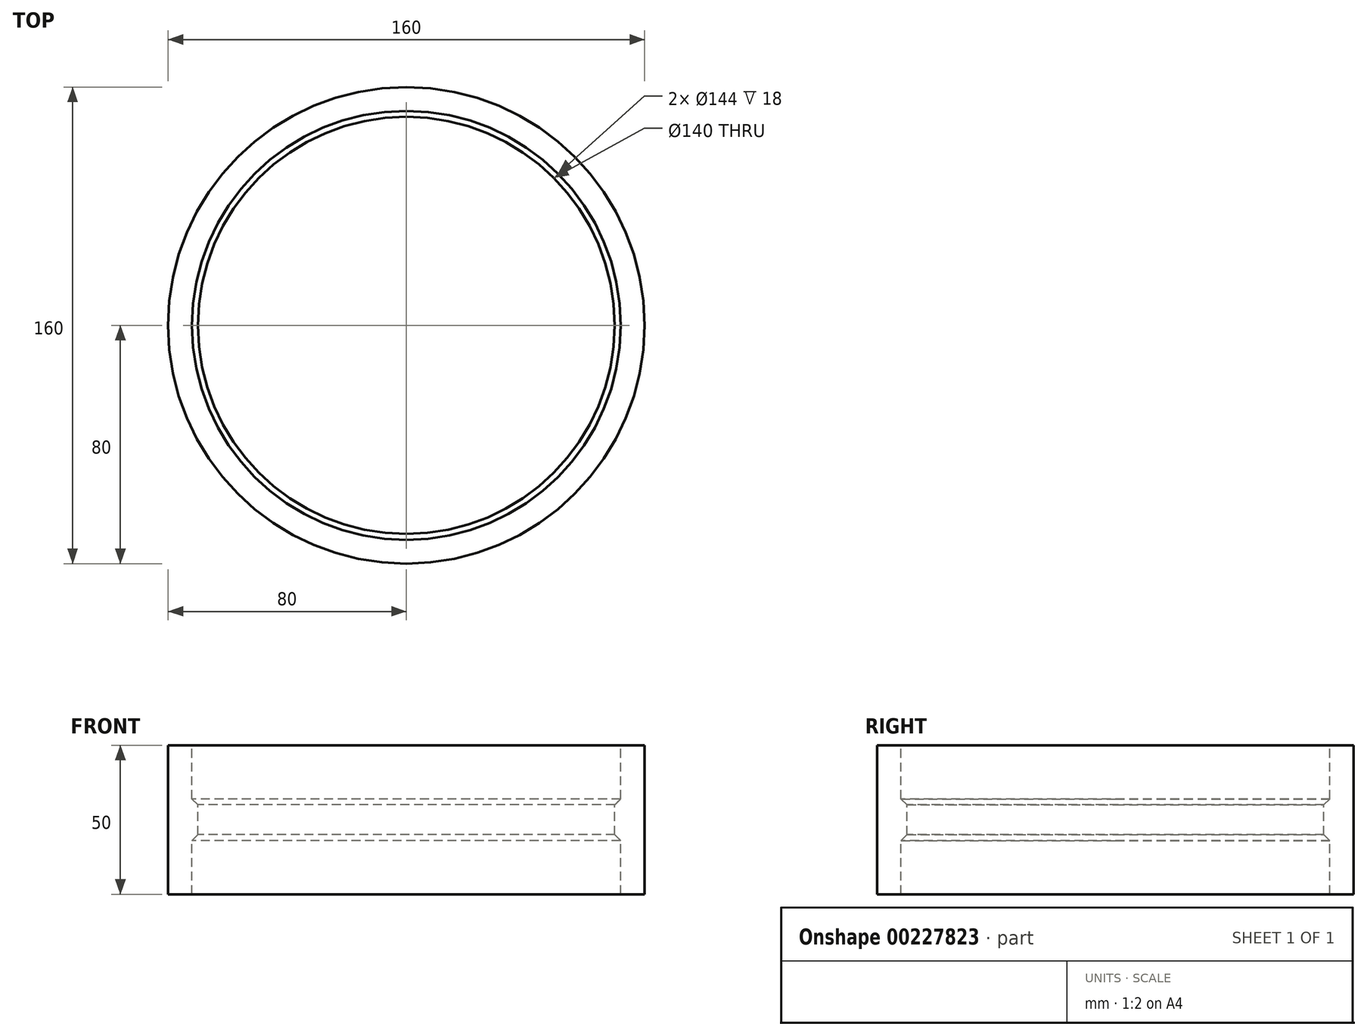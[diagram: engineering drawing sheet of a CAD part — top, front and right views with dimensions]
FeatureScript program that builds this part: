
annotation { "Feature Type Name" : "Feature", "Feature Type Description" : "" }
export const myFeature = defineFeature(function(context is Context, id is Id, definition is map)
    precondition{}
    {
        {
            var Q0;
            Q0=qCreatedBy(makeId("Front.planeOp"),FACE);
            var sketch = newSketch(context, id + "F0", { "sketchPlane" : qUnion([Q0])});
            skLineSegment(sketch, "E0", {"start": v(-80, 25) * mm, "end": v(-80, -25) * mm});
            skLineSegment(sketch, "E1", {"start": v(-72, 25) * mm, "end": v(-80, 25) * mm});
            skLineSegment(sketch, "E2", {"start": v(-72, 25) * mm, "end": v(-72, 7) * mm});
            skLineSegment(sketch, "E3", {"start": v(-70, 5) * mm, "end": v(-70, -5) * mm});
            skLineSegment(sketch, "E4", {"start": v(-80, -25) * mm, "end": v(-72, -25) * mm});
            skLineSegment(sketch, "E5.trimOffspring", {"start": v(-72, -7) * mm, "end": v(-72, -25) * mm});
            skPoint(sketch, "E6.orphan", {"position": v(0, -25) * mm});
            skPoint(sketch, "E7.start.orphan", {"position": v(-30.76, -25) * mm});
            skLineSegment(sketch, "E8", {"start": v(0, 18.56) * mm, "end": v(0, -66.84) * mm});
            skLineSegment(sketch, "E9", {"start": v(-72, 7) * mm, "end": v(-70, 5) * mm});
            skLineSegment(sketch, "E10", {"start": v(-72, -7) * mm, "end": v(-70, -5) * mm});
            skSolve(sketch);
        }
        {
            var Q0;
            Q0 = qSketchRegion(id + "F0", true);
            var Q1;
            Q1=sQuery(id+"F0.wireOp",EDGE,"E8");
            revolve(context, id + "F1", {"entities" : qUnion([Q0]), "axis" : qUnion([Q1]), "revolveType" : RevolveType.FULL});
        }
        {
            var Q0;
            Q0=qCreatedBy(makeId("Top.planeOp"),FACE);
            var sketch = newSketch(context, id + "F2", { "sketchPlane" : qUnion([Q0])});
            skLineSegment(sketch, "E11", {"start": v(-19.9, -15) * mm, "end": v(24.27, -15) * mm});
            skPoint(sketch, "E12", {"position": v(0, -15) * mm});
            skSolve(sketch);
        }
    });
